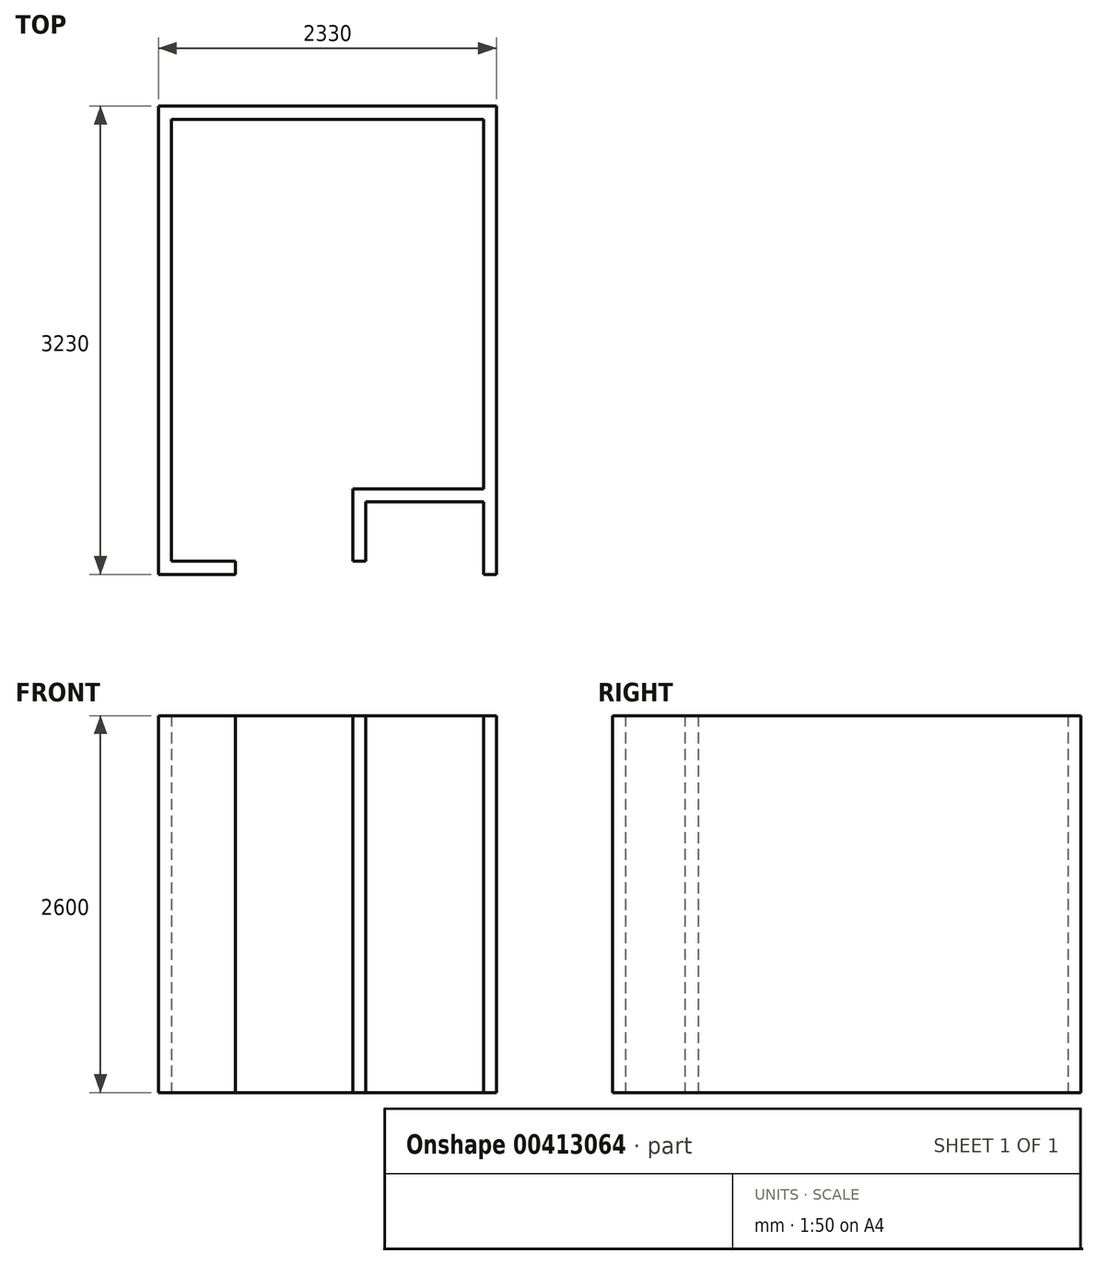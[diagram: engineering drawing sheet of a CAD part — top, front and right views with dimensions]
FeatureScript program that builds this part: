
annotation { "Feature Type Name" : "Feature", "Feature Type Description" : "" }
export const myFeature = defineFeature(function(context is Context, id is Id, definition is map)
    precondition{}
    {
        {
            var Q0;
            Q0=qCreatedBy(makeId("Top.planeOp"),FACE);
            var sketch = newSketch(context, id + "F0", { "sketchPlane" : qUnion([Q0])});
            skLineSegment(sketch, "E0.bottom", {"start": v(0, 0) * mm, "end": v(2240, 0) * mm, "construction": true});
            skLineSegment(sketch, "E0.left", {"start": v(0, 0) * mm, "end": v(0, -3140) * mm, "construction": true});
            skLineSegment(sketch, "E0.right", {"start": v(2240, 0) * mm, "end": v(2240, -3040) * mm, "construction": true});
            skLineSegment(sketch, "E1.top", {"start": v(2240, -2640) * mm, "end": v(1340, -2640) * mm, "construction": true});
            skLineSegment(sketch, "E1.right", {"start": v(1340, -3095) * mm, "end": v(1340, -2640) * mm, "construction": true});
            skLineSegment(sketch, "E2.bottom", {"start": v(0, -3140) * mm, "end": v(440, -3140) * mm, "construction": true});
            skLineSegment(sketch, "E2.right", {"start": v(440, -3140) * mm, "end": v(440, -2640) * mm, "construction": true});
            skLineSegment(sketch, "E3", {"start": v(440, -2640) * mm, "end": v(1340, -2640) * mm, "construction": true});
            skLineSegment(sketch, "E4", {"start": v(440, -2640) * mm, "end": v(440, 0) * mm, "construction": true});
            skLineSegment(sketch, "E5.0", {"start": v(2195, -45) * mm, "end": v(2195, -2595) * mm});
            skLineSegment(sketch, "E5.2", {"start": v(45, -3095) * mm, "end": v(485, -3095) * mm});
            skLineSegment(sketch, "E5.3", {"start": v(45, -45) * mm, "end": v(45, -3095) * mm});
            skLineSegment(sketch, "E5.4", {"start": v(45, -45) * mm, "end": v(2195, -45) * mm});
            skLineSegment(sketch, "E6.0", {"start": v(2285, 45) * mm, "end": v(2285, -3185) * mm});
            skLineSegment(sketch, "E6.1", {"start": v(485, -3185) * mm, "end": v(485, -3095) * mm});
            skLineSegment(sketch, "E6.2", {"start": v(-45, -3185) * mm, "end": v(485, -3185) * mm});
            skLineSegment(sketch, "E6.3", {"start": v(-45, 45) * mm, "end": v(-45, -3185) * mm});
            skLineSegment(sketch, "E6.4", {"start": v(-45, 45) * mm, "end": v(2285, 45) * mm});
            skLineSegment(sketch, "E7.0", {"start": v(2195, -2685) * mm, "end": v(1385, -2685) * mm});
            skLineSegment(sketch, "E7.1", {"start": v(1385, -3095) * mm, "end": v(1385, -2685) * mm});
            skLineSegment(sketch, "E8.0", {"start": v(2195, -2595) * mm, "end": v(1295, -2595) * mm});
            skLineSegment(sketch, "E8.1", {"start": v(1295, -3095) * mm, "end": v(1295, -2595) * mm});
            skLineSegment(sketch, "E9", {"start": v(1295, -3095) * mm, "end": v(1385, -3095) * mm});
            skLineSegment(sketch, "E10", {"start": v(2195, -3185) * mm, "end": v(2285, -3185) * mm});
            skLineSegment(sketch, "E11.trimOffspring", {"start": v(2195, -2685) * mm, "end": v(2195, -3185) * mm});
            skSolve(sketch);
        }
        {
            var Q0;
            Q0 = qSketchRegion(id + "F0", true);
            extrude(context, id + "F1", {"entities" : qUnion([Q0]), "depth" : 2600 * mm});
        }
    });
